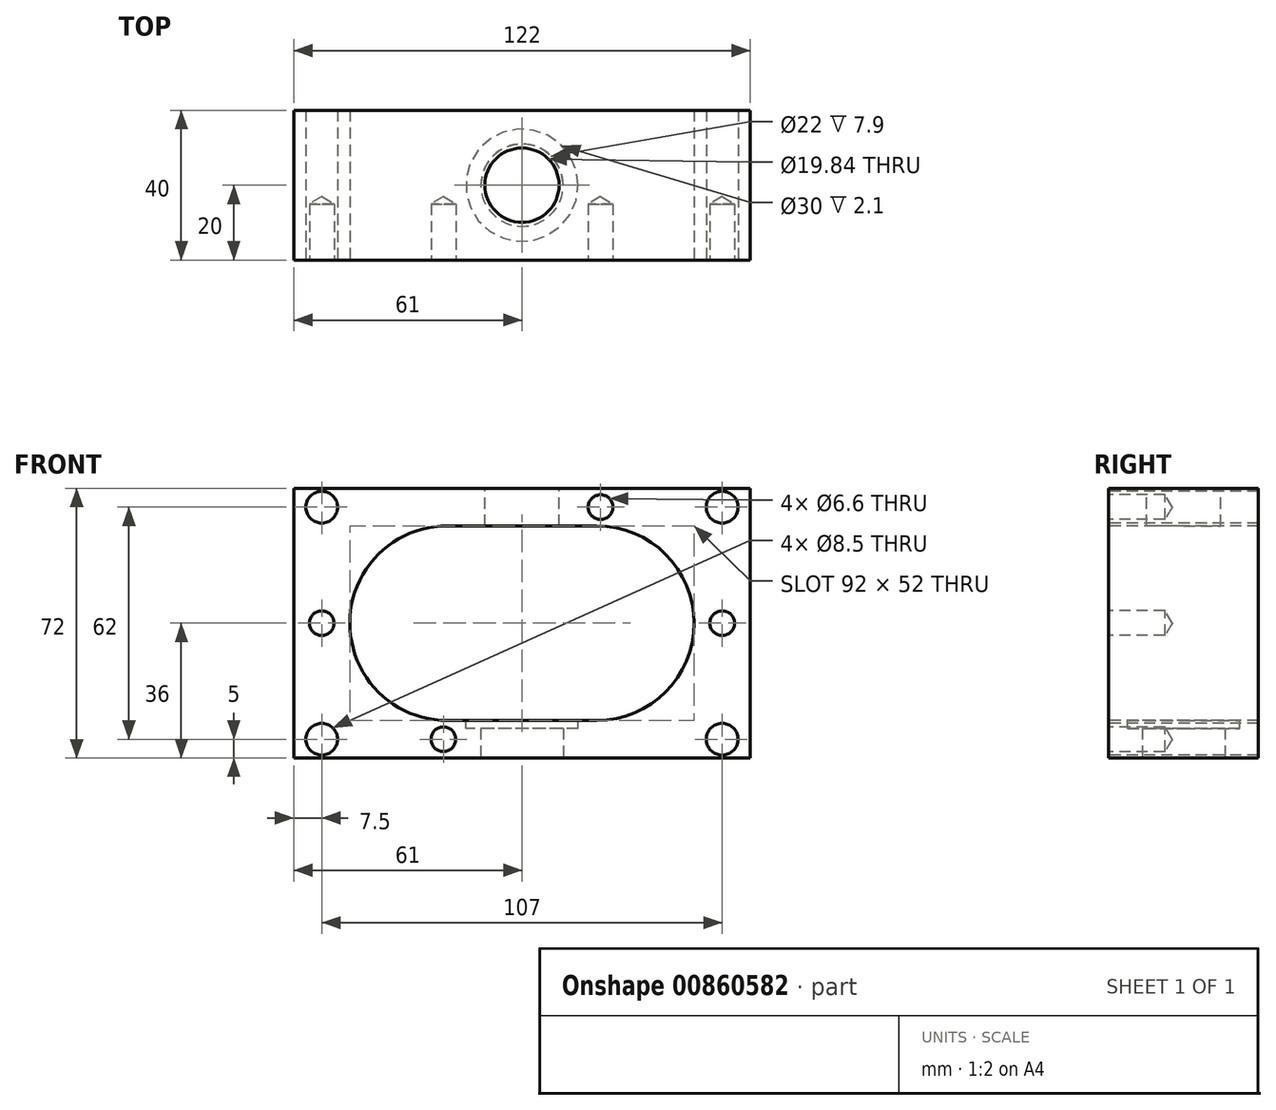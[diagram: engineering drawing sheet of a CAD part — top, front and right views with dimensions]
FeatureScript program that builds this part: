
annotation { "Feature Type Name" : "Feature", "Feature Type Description" : "" }
export const myFeature = defineFeature(function(context is Context, id is Id, definition is map)
    precondition{}
    {
        {
            var Q0;
            Q0=qCreatedBy(makeId("Front.planeOp"),FACE);
            var sketch = newSketch(context, id + "F0", { "sketchPlane" : qUnion([Q0])});
            skLineSegment(sketch, "E0.bottom", {"start": v(61, 36) * mm, "end": v(-61, 36) * mm});
            skLineSegment(sketch, "E0.top", {"start": v(61, -36) * mm, "end": v(-61, -36) * mm});
            skLineSegment(sketch, "E0.left", {"start": v(61, 36) * mm, "end": v(61, -36) * mm});
            skLineSegment(sketch, "E0.right", {"start": v(-61, 36) * mm, "end": v(-61, -36) * mm});
            skPoint(sketch, "E0.middle", {"position": v(0, 0) * mm});
            skArc(sketch, "E1", {"start": v(-20, 26) * mm, "mid": v(-46, -0.04) * mm, "end": v(-19.93, -26) * mm});
            skArc(sketch, "E2", {"start": v(20, -26) * mm, "mid": v(46, 0) * mm, "end": v(20, 26) * mm});
            skLineSegment(sketch, "E3", {"start": v(-20, 26) * mm, "end": v(20, 26) * mm});
            skLineSegment(sketch, "E4", {"start": v(-19.93, -26) * mm, "end": v(20, -26) * mm});
            skPoint(sketch, "E5", {"position": v(21, 31) * mm});
            skPoint(sketch, "E6", {"position": v(-21, -31) * mm});
            skPoint(sketch, "E7", {"position": v(53.5, 0) * mm});
            skPoint(sketch, "E8", {"position": v(-53.5, 0) * mm});
            skPoint(sketch, "E9", {"position": v(53.5, 31) * mm});
            skPoint(sketch, "E10", {"position": v(53.5, -31) * mm});
            skPoint(sketch, "E11", {"position": v(-53.5, -31) * mm});
            skPoint(sketch, "E12", {"position": v(-53.5, 31) * mm});
            skSolve(sketch);
        }
        {
            var Q0;
            Q0 = qSketchRegion(id + "F0", true);
            extrude(context, id + "F1", {"entities" : qUnion([Q0]), "oppositeDirection" : true, "depth" : 40 * mm, "offsetDistance" : 25.4 * mm});
        }
        {
            var Q0;
            Q0=sQuery(id+"F0.wireOp",VERTEX,"E5");
            var Q1;
            Q1=sQuery(id+"F0.wireOp",VERTEX,"E7");
            var Q2;
            Q2=sQuery(id+"F0.wireOp",VERTEX,"E6");
            var Q3;
            Q3=sQuery(id+"F0.wireOp",VERTEX,"E8");
            var Q4;
            Q4=makeQuery(id+"F1.opExtrude","SWEPT_BODY",BODY,{"disambiguationData":[OSD([sQuery(id+"F0.wireOp",EDGE,"E0.bottom"),sQuery(id+"F0.wireOp",EDGE,"E0.top"),sQuery(id+"F0.wireOp",EDGE,"E0.left"),sQuery(id+"F0.wireOp",EDGE,"E0.right"),sQuery(id+"F0.wireOp",EDGE,"E1"),sQuery(id+"F0.wireOp",EDGE,"E2"),sQuery(id+"F0.wireOp",EDGE,"E3"),sQuery(id+"F0.wireOp",EDGE,"E4")])]});
            hole(context, id + "F2", {"style" : HoleStyle.SIMPLE, "endStyle" : HoleEndStyle.BLIND, "standardTappedOrClearance" : lookupTablePath({ "fit" : "Normal", "standard" : "ISO", "size" : "M6", "type" : "Clearance" }), "standardBlindInLast" : lookupTablePath({ "fit" : "Standard", "standard" : "ISO", "size" : "M6", "type" : "Clearance" }), "holeDiameter" : 6.6 * mm, "majorDiameter" : 6.35 * mm, "holeDepth" : 15 * mm, "isTappedThrough" : true, "tappedDepth" : 12.7 * mm, "tapClearance" : 3, "locations" : qUnion([Q0, Q1, Q2, Q3]), "scope" : qUnion([Q4])});
        }
        {
            var Q0;
            Q0=sQuery(id+"F0.wireOp",VERTEX,"E12");
            var Q1;
            Q1=sQuery(id+"F0.wireOp",VERTEX,"E11");
            var Q2;
            Q2=sQuery(id+"F0.wireOp",VERTEX,"E9");
            var Q3;
            Q3=sQuery(id+"F0.wireOp",VERTEX,"E10");
            var Q4;
            Q4=makeQuery(id+"F1.opExtrude","SWEPT_BODY",BODY,{"disambiguationData":[OSD([sQuery(id+"F0.wireOp",EDGE,"E0.bottom"),sQuery(id+"F0.wireOp",EDGE,"E0.top"),sQuery(id+"F0.wireOp",EDGE,"E0.left"),sQuery(id+"F0.wireOp",EDGE,"E0.right"),sQuery(id+"F0.wireOp",EDGE,"E1"),sQuery(id+"F0.wireOp",EDGE,"E2"),sQuery(id+"F0.wireOp",EDGE,"E3"),sQuery(id+"F0.wireOp",EDGE,"E4")])]});
            hole(context, id + "F3", {"style" : HoleStyle.SIMPLE, "endStyle" : HoleEndStyle.THROUGH, "standardTappedOrClearance" : lookupTablePath({ "standard" : "ISO", "size" : "8.5", "type" : "Drilled" }), "standardBlindInLast" : lookupTablePath({ "standard" : "ISO", "size" : "8.5", "type" : "Drilled" }), "holeDiameter" : 8.5 * mm, "majorDiameter" : 6.35 * mm, "isTappedThrough" : true, "tappedDepth" : 12.7 * mm, "tapClearance" : 3, "locations" : qUnion([Q0, Q1, Q2, Q3]), "scope" : qUnion([Q4])});
        }
        {
            var Q0;
            Q0=makeQuery(id+"F1.opExtrude","SWEPT_FACE",FACE,{"disambiguationData":[OSD([sQuery(id+"F0.wireOp",EDGE,"E0.bottom")])]});
            var sketch = newSketch(context, id + "F4", { "sketchPlane" : qUnion([Q0])});
            skPoint(sketch, "E13", {"position": v(0, 20) * mm});
            skSolve(sketch);
        }
        {
            var Q0;
            Q0=sQuery(id+"F4.wireOp",VERTEX,"E13");
            var Q1;
            Q1=makeQuery(id+"F1.opExtrude","SWEPT_BODY",BODY,{"disambiguationData":[OSD([sQuery(id+"F0.wireOp",EDGE,"E0.bottom"),sQuery(id+"F0.wireOp",EDGE,"E0.top"),sQuery(id+"F0.wireOp",EDGE,"E0.left"),sQuery(id+"F0.wireOp",EDGE,"E0.right"),sQuery(id+"F0.wireOp",EDGE,"E1"),sQuery(id+"F0.wireOp",EDGE,"E2"),sQuery(id+"F0.wireOp",EDGE,"E3"),sQuery(id+"F0.wireOp",EDGE,"E4")])]});
            hole(context, id + "F5", {"style" : HoleStyle.SIMPLE, "endStyle" : HoleEndStyle.BLIND, "standardTappedOrClearance" : lookupTablePath({ "fit" : "Normal (ASME)", "standard" : "ANSI", "size" : "3/4", "type" : "Clearance" }), "standardBlindInLast" : lookupTablePath({ "fit" : "Free", "standard" : "ANSI", "size" : "3/4", "type" : "Clearance" }), "holeDiameter" : 19.84 * mm, "majorDiameter" : 5 * mm, "holeDepth" : 15 * mm, "isTappedThrough" : true, "tappedDepth" : 12.7 * mm, "tapClearance" : 3, "locations" : qUnion([Q0]), "scope" : qUnion([Q1])});
        }
        {
            var Q0;
            Q0=makeQuery(id+"F1.opExtrude","SWEPT_FACE",FACE,{"disambiguationData":[OSD([sQuery(id+"F0.wireOp",EDGE,"E0.top")])]});
            var sketch = newSketch(context, id + "F6", { "sketchPlane" : qUnion([Q0])});
            skCircle(sketch, "E14", {"center": v(0, -20) * mm, "radius": 11 * mm});
            skSolve(sketch);
        }
        {
            var Q0;
            Q0 = qSketchRegion(id + "F6", true);
            extrude(context, id + "F7", {"entities" : qUnion([Q0]), "operationType" : NewBodyOperationType.REMOVE, "oppositeDirection" : true, "depth" : 25 * mm, "offsetDistance" : 25 * mm});
        }
        {
            var Q0;
            Q0=makeQuery(id+"F1.opExtrude","SWEPT_FACE",FACE,{"disambiguationData":[OSD([sQuery(id+"F0.wireOp",EDGE,"E4")])]});
            var sketch = newSketch(context, id + "F8", { "sketchPlane" : qUnion([Q0])});
            skCircle(sketch, "E15", {"center": v(0, 20) * mm, "radius": 15 * mm});
            skSolve(sketch);
        }
        {
            var Q0;
            Q0 = qSketchRegion(id + "F8", true);
            extrude(context, id + "F9", {"entities" : qUnion([Q0]), "operationType" : NewBodyOperationType.REMOVE, "oppositeDirection" : true, "depth" : 2.1 * mm, "offsetDistance" : 25 * mm});
        }
    });
